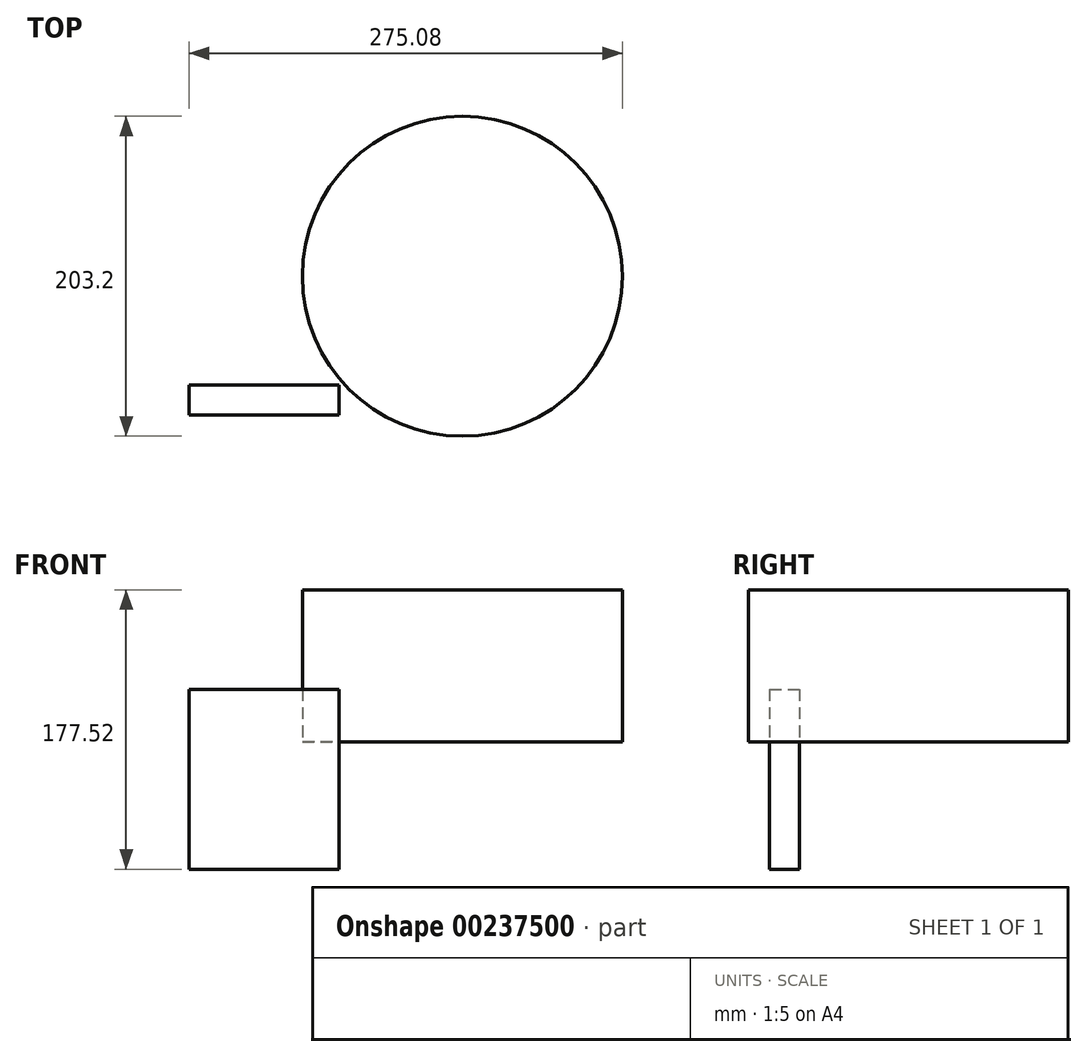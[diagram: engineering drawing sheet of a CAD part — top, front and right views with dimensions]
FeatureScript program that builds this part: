
annotation { "Feature Type Name" : "Feature", "Feature Type Description" : "" }
export const myFeature = defineFeature(function(context is Context, id is Id, definition is map)
    precondition{}
    {
        {
            var Q0;
            Q0=qCreatedBy(makeId("Front.planeOp"),FACE);
            var sketch = newSketch(context, id + "F0", { "sketchPlane" : qUnion([Q0])});
            skLineSegment(sketch, "E0.bottom", {"start": v(-15.94, 33.3) * mm, "end": v(-111.2, 33.3) * mm});
            skLineSegment(sketch, "E0.top", {"start": v(-15.94, -81) * mm, "end": v(-111.2, -81) * mm});
            skLineSegment(sketch, "E0.left", {"start": v(-15.94, 33.3) * mm, "end": v(-15.94, -81) * mm});
            skLineSegment(sketch, "E0.right", {"start": v(-111.2, 33.3) * mm, "end": v(-111.2, -81) * mm});
            skSolve(sketch);
        }
        {
            var Q0;
            Q0 = qSketchRegion(id + "F0", true);
            extrude(context, id + "F1", {"entities" : qUnion([Q0]), "depth" : 19.05 * mm});
        }
        {
            var Q0;
            Q0=qCreatedBy(makeId("Top.planeOp"),FACE);
            var sketch = newSketch(context, id + "F2", { "sketchPlane" : qUnion([Q0])});
            skCircle(sketch, "E1", {"center": v(62.29, 68.99) * mm, "radius": 101.6 * mm});
            skSolve(sketch);
        }
        {
            var Q0;
            Q0 = qSketchRegion(id + "F2", true);
            extrude(context, id + "F3", {"entities" : qUnion([Q0]), "depth" : 96.52 * mm});
        }
    });
